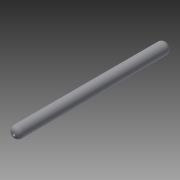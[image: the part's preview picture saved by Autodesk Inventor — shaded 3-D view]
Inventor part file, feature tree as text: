
AUTODESK INVENTOR PART (.ipt)
format: ipt  version: 2013 (Build 170138000, 138)  size: 82,432 bytes
history: native  units: in
note: dims shown in document units (in); Inventor stores cm internally (conversion verified against a paired STEP export)
features: extrude x1, fillet x1, sketch x1
ambient origin geometry x8: Origin, YZ Plane, XZ Plane, XY Plane, X Axis, Y Axis, Z Axis, Center Point
bodies: Solid1 (feature_tree)
feature tree (3):
  extrude  "Extrusion1"  Depth=0.75in
  fillet  "Fillet1"  Radius=33.25in
  sketch  "Sketch1"  dims[d0=2.5in d1=0.75in d2=33.25in d3=0.0in d4=1.0in]
